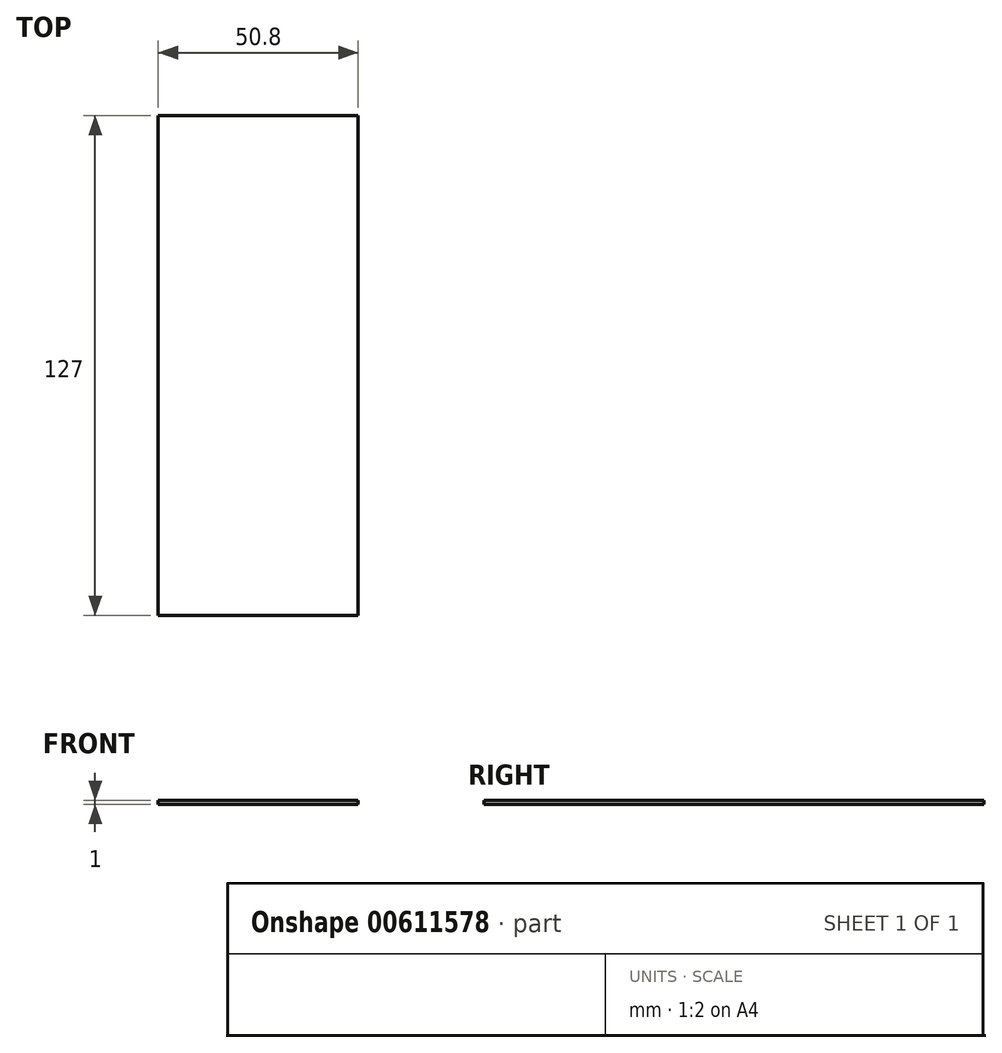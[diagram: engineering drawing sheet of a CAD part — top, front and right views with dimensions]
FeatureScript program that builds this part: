
annotation { "Feature Type Name" : "Feature", "Feature Type Description" : "" }
export const myFeature = defineFeature(function(context is Context, id is Id, definition is map)
    precondition{}
    {
        {
            var Q0;
            Q0=qCreatedBy(makeId("Top.planeOp"),FACE);
            var sketch = newSketch(context, id + "F0", { "sketchPlane" : qUnion([Q0])});
            skLineSegment(sketch, "E0.bottom", {"start": v(-25.4, 63.5) * mm, "end": v(25.4, 63.5) * mm});
            skLineSegment(sketch, "E0.top", {"start": v(-25.4, -63.5) * mm, "end": v(25.4, -63.5) * mm});
            skLineSegment(sketch, "E0.left", {"start": v(-25.4, 63.5) * mm, "end": v(-25.4, -63.5) * mm});
            skLineSegment(sketch, "E0.right", {"start": v(25.4, 63.5) * mm, "end": v(25.4, -63.5) * mm});
            skSolve(sketch);
        }
        {
            var Q0;
            Q0=makeQuery(id+"F0.imprint","IMPRINT",FACE,{"disambiguationData":[TD([[makeQuery(id+"F0.imprint","IMPRINT",EDGE,{"derivedFrom":sQuery(id+"F0.wireOp",EDGE,"E0.bottom")}),-1.0]])]});
            extrude(context, id + "F1", {"entities" : qUnion([Q0]), "depth" : 1 * mm, "offsetDistance" : 25.4 * mm});
        }
    });
